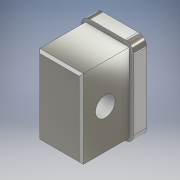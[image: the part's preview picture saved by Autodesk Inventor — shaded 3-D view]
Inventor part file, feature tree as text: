
AUTODESK INVENTOR PART (.ipt)
format: ipt  version: 2017 (Build 210142000, 142)  size: 178,176 bytes
history: native  units: mm
features: extrude x4, sketch x4, fillet x2, chamfer x1, projected_geometry x1
ambient origin geometry x8: Origin, YZ Plane, XZ Plane, XY Plane, X Axis, Y Axis, Z Axis, Center Point
bodies: Solid1 (feature_tree)
feature tree (12):
  extrude  "Extrusion1"  Depth=3.0mm TaperAngle=0.0deg
  extrude  "Extrusion4"  Depth=14.0mm
  extrude  "Extrusion5"  Depth=9.0mm
  extrude  "Extrusion6"  Depth=3.0mm
  chamfer  "Chamfer1"  Distance=9.0mm
  fillet  "Fillet1"  Radius=3.0mm
  fillet  "Fillet2"  Radius=3.0mm
  sketch  "Sketch1"  dims[d0=12.0mm d1=20.0mm d2=1.0mm d3=5.0mm d4=10.0mm d5=18.0mm d6=3.0mm d7=0.0mm]
  sketch  "Sketch2"  dims[d19=14.0mm d20=0.0mm d21=4.5mm]
  sketch  "Sketch5"  dims[d22=0.0mm d23=0.0mm]
  projected_geometry  "Projected Loop3"
  sketch  "Sketch6"  dims[d24=3.0mm d25=14.0mm d26=3.0mm d27=6.0mm d28=14.0mm d29=9.0mm d30=3.0mm d31=9.0mm d32=3.0mm d33=3.0mm d34=0.0mm d35=0.0mm d36=1.0mm d37=10.0mm d38=18.0mm d39=11.0mm d40=19.0mm d41=11.0mm d42=1.0mm d43=9.0mm d44=5.5mm d45=0.5mm d46=2.0mm d47=45.0deg d48=2.0mm d49=2.0mm]
